# Revit family: rba-bim-rba8847-428(Recovery)
name_source: partatom
category: Plumbing Fixtures
revit_build: Autodesk Revit 2018 (Build: 20170223_1515(x64)
units: mm (PartAtom-declared; Revit-internal decimal feet)

## family parameters
Always vertical = Yes
Cut with Voids When Loaded = No
OmniClass Number = 23.45.00.00
OmniClass Title = Sanitary, Laundry, and Cleaning Equipment
Part Type = Normal
Room Calculation Point = No
Round Connector Dimension = Use Diameter
Shared = No
Work Plane-Based = No

## types (2) — shared parameters
Manufacturer = RBA Group
Materials and Finishes = Type 304 Stainless Steel

## per-type parameters (varying)
| type | Description | H | Modified Issue | URL |
| RBA8847-100 | Wall Faced WC Pan with Cistern | 845 mm |  | www.rba.com.au/toilets-urinals/toilets |
| RBA8847-428 | Wall Faced WC Pan with Cistern for Disable use | 880 mm  [stored 2.88714 ft] | 20200526.01 | www.rba.com.au |

note: column(s) folded — value = type name in every type: Model

note: [stored X ft] marks values corroborated as IEEE doubles in the binary element streams (Revit-internal decimal feet)

## geometry (parser evidence)
native form markers: Blend x2, Sweep x3
no freeform markers — native parametric forms only
